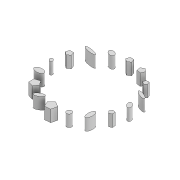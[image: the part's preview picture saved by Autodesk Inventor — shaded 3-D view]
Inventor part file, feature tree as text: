
AUTODESK INVENTOR PART (.ipt)
format: ipt  version: 2021 (Build 250183000, 183)  size: 167,424 bytes
history: native  units: in
note: dims shown in document units (in); Inventor stores cm internally (conversion verified against a paired STEP export)
features: extrude x1, sketch x1
ambient origin geometry x8: Origin, YZ Plane, XZ Plane, XY Plane, X Axis, Y Axis, Z Axis, Center Point
bodies: Solid1 (feature_tree)
feature tree (2):
  extrude  "Extrusion1"  Depth=118.1102in TaperAngle=360.0deg
  sketch  "Sketch1"  dims[d0=787.4016in d1=6.2992in d3=360.0deg d5=118.1102in d6=0.0in]
